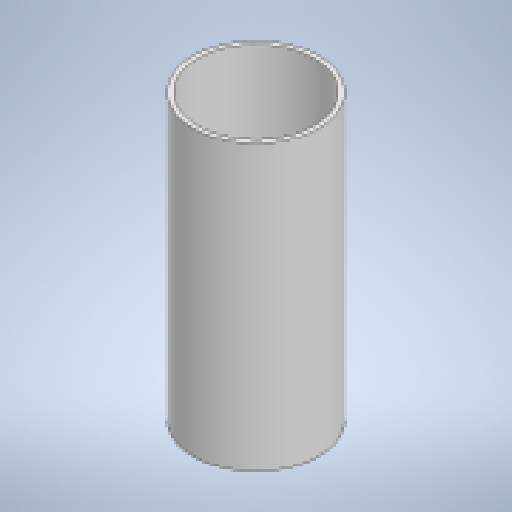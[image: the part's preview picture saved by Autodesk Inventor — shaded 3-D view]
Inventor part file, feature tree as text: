
AUTODESK INVENTOR PART (.ipt)
format: ipt  version: 2025 (Build 290162010, 162A)  size: 212,992 bytes
history: native  units: mm
features: extrude x1, sketch x1
ambient origin geometry x8: Origin, YZ Plane, XZ Plane, XY Plane, X Axis, Y Axis, Z Axis, Center Point
bodies: Solid1 (feature_tree)
feature tree (2):
  extrude  "Extrusion1"  Depth=300.0mm
  sketch  "Sketch1"  dims[d0=133.0mm d1=5.0mm d2=300.0mm d3=0.0mm]
